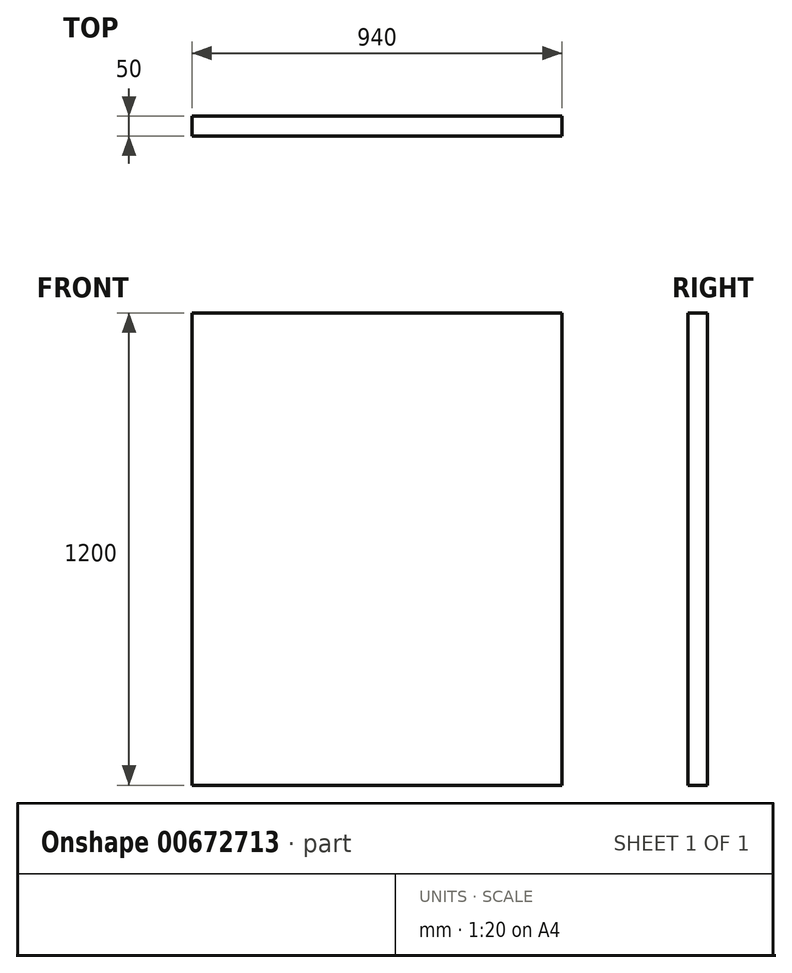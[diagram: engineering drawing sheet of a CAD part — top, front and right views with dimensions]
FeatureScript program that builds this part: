
annotation { "Feature Type Name" : "Feature", "Feature Type Description" : "" }
export const myFeature = defineFeature(function(context is Context, id is Id, definition is map)
    precondition{}
    {
        {
            var Q0;
            Q0=qCreatedBy(makeId("Front.planeOp"),FACE);
            var sketch = newSketch(context, id + "F0", { "sketchPlane" : qUnion([Q0])});
            skLineSegment(sketch, "E0.bottom", {"start": v(0, 0) * mm, "end": v(-940, 0) * mm});
            skLineSegment(sketch, "E0.top", {"start": v(0, 1200) * mm, "end": v(-940, 1200) * mm});
            skLineSegment(sketch, "E0.left", {"start": v(0, 0) * mm, "end": v(0, 1200) * mm});
            skLineSegment(sketch, "E0.right", {"start": v(-940, 0) * mm, "end": v(-940, 1200) * mm});
            skSolve(sketch);
        }
        {
            var Q0;
            Q0=makeQuery(id+"F0.imprint","IMPRINT",FACE,{"disambiguationData":[TD([[makeQuery(id+"F0.imprint","IMPRINT",EDGE,{"derivedFrom":sQuery(id+"F0.wireOp",EDGE,"E0.bottom")}),-1.0]])]});
            extrude(context, id + "F1", {"entities" : qUnion([Q0]), "depth" : 50 * mm, "offsetDistance" : 25 * mm});
        }
    });
